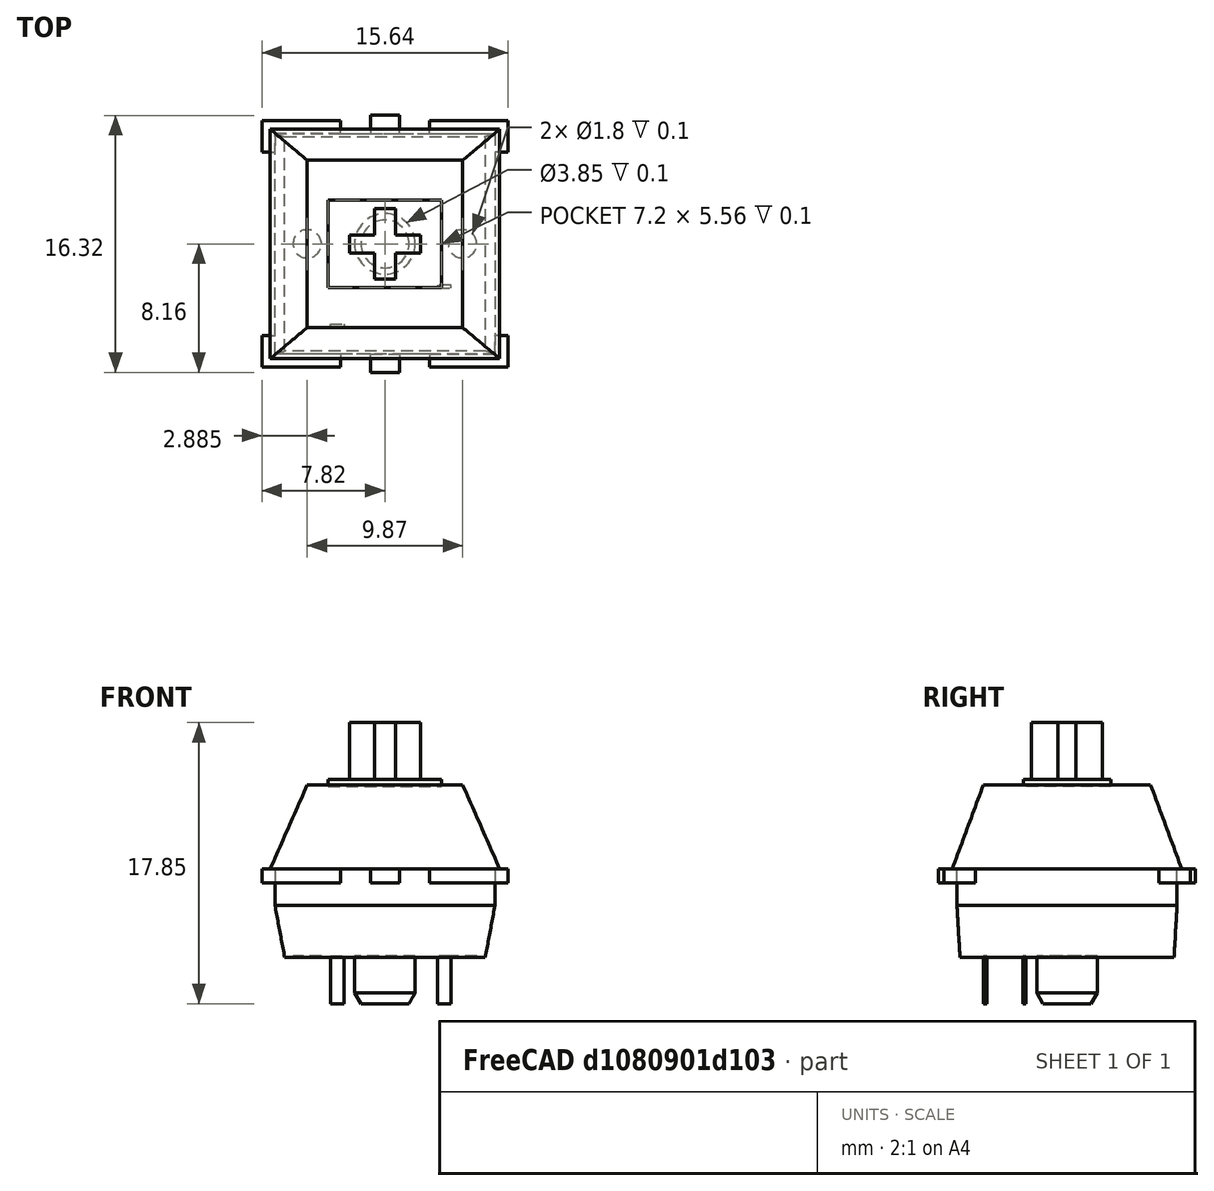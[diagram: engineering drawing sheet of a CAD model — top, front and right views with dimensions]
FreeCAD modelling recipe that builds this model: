
FCSTD DOCUMENT  (FreeCAD 0.19R19285 (Git))
Label: cherry-mx-basic
License: CreativeCommons Attribution-ShareAlike
LicenseURL: http://creativecommons.org/licenses/by-sa/4.0/
objects: Sketcher::SketchObject×20, PartDesign::Pad×7, PartDesign::Pocket×4, PartDesign::Body×4, PartDesign::Plane×3, PartDesign::AdditiveLoft×3, PartDesign::Mirrored×3, PartDesign::MultiTransform×1, Mesh::Feature×1, Part::Feature×1, App::Part×1
note: 60 computed .brp shape members not serialized (recipe doc carries the construction recipe); baked Part::Feature solids carry a one-line shape summary decoded from their .brp

FEATURE [Sketcher::SketchObject] Sketch  label="Master_h"
  MapMode = 5
  Support = -> [XY_Plane]
  sketch-geometry (31):
    g0: LineSegment StartX=7.29 StartY=7.29 StartZ=0 EndX=7.29 EndY=-7.29 EndZ=0
    g1: LineSegment StartX=7.29 StartY=-7.29 StartZ=0 EndX=-7.29 EndY=-7.29 EndZ=0
    g2: LineSegment StartX=-7.29 StartY=-7.29 StartZ=0 EndX=-7.29 EndY=7.29 EndZ=0
    g3: LineSegment StartX=-7.29 StartY=7.29 StartZ=0 EndX=7.29 EndY=7.29 EndZ=0
    g4: LineSegment [constr] StartX=-7.29 StartY=7.29 StartZ=0 EndX=-6.99 EndY=6.99 EndZ=0
    g5: LineSegment StartX=-6.99 StartY=6.99 StartZ=0 EndX=6.99 EndY=6.99 EndZ=0
    g6: LineSegment StartX=6.99 StartY=6.99 StartZ=0 EndX=6.99 EndY=-6.99 EndZ=0
    g7: LineSegment StartX=6.99 StartY=-6.99 StartZ=0 EndX=-6.99 EndY=-6.99 EndZ=0
    g8: LineSegment StartX=-6.99 StartY=-6.99 StartZ=0 EndX=-6.99 EndY=6.99 EndZ=0
    g9: LineSegment StartX=-6.37 StartY=6.8 StartZ=0 EndX=6.37 EndY=6.8 EndZ=0
    g10: LineSegment StartX=6.37 StartY=6.8 StartZ=0 EndX=6.37 EndY=-6.8 EndZ=0
    g11: LineSegment StartX=6.37 StartY=-6.8 StartZ=0 EndX=-6.37 EndY=-6.8 EndZ=0
    g12: LineSegment StartX=-6.37 StartY=-6.8 StartZ=0 EndX=-6.37 EndY=6.8 EndZ=0
    g13: LineSegment StartX=-4.935 StartY=5.31 StartZ=0 EndX=4.935 EndY=5.31 EndZ=0
    g14: LineSegment StartX=4.935 StartY=5.31 StartZ=0 EndX=4.935 EndY=-5.31 EndZ=0
    g15: LineSegment StartX=4.935 StartY=-5.31 StartZ=0 EndX=-4.935 EndY=-5.31 EndZ=0
    g16: LineSegment StartX=-4.935 StartY=-5.31 StartZ=0 EndX=-4.935 EndY=5.31 EndZ=0
    g17: LineSegment StartX=-3.6 StartY=2.78 StartZ=0 EndX=3.6 EndY=2.78 EndZ=0
    g18: LineSegment StartX=3.6 StartY=2.78 StartZ=0 EndX=3.6 EndY=-2.78 EndZ=0
    g19: LineSegment StartX=3.6 StartY=-2.78 StartZ=0 EndX=-3.6 EndY=-2.78 EndZ=0
    g20: LineSegment StartX=-3.6 StartY=-2.78 StartZ=0 EndX=-3.6 EndY=2.78 EndZ=0
    g21: LineSegment StartX=-0.91 StartY=-6.99 StartZ=0 EndX=0.91 EndY=-6.99 EndZ=0
    g22: LineSegment StartX=0.91 StartY=-6.99 StartZ=0 EndX=0.91 EndY=-8.165 EndZ=0
    g23: LineSegment StartX=0.91 StartY=-8.165 StartZ=0 EndX=-0.91 EndY=-8.165 EndZ=0
    g24: LineSegment StartX=-0.91 StartY=-8.165 StartZ=0 EndX=-0.91 EndY=-6.99 EndZ=0
    g25: LineSegment StartX=-7.82 StartY=-5.82 StartZ=0 EndX=-2.82 EndY=-5.82 EndZ=0
    g26: LineSegment StartX=-2.82 StartY=-5.82 StartZ=0 EndX=-2.82 EndY=-7.82 EndZ=0
    g27: LineSegment StartX=-2.82 StartY=-7.82 StartZ=0 EndX=-7.82 EndY=-7.82 EndZ=0
    g28: LineSegment StartX=-7.82 StartY=-7.82 StartZ=0 EndX=-7.82 EndY=-5.82 EndZ=0
    g29: Circle CenterX=0 CenterY=0 CenterZ=0 NormalX=0 NormalY=0 NormalZ=1 AngleXU=0 Radius=1.925
    g30: Circle CenterX=4.935 CenterY=0 CenterZ=0 NormalX=0 NormalY=0 NormalZ=1 AngleXU=0 Radius=0.8
  constraints (85):
    c: Coincident(g0,g1)
    c: Coincident(g1,g2)
    c: Horizontal(g1)
    c: Vertical(g0)
    c: Vertical(g2)
    c: DistanceX(g2,g0) = 14.58
    c: Symmetric(g2,g0,g-1)
    c: Coincident(g3,g2)
    c: Coincident(g3,g0)
    c: Horizontal(g3)
    c: Equal(g3,g0)
    c: Coincident(g4,g2)
    c: Coincident(g5,g6)
    c: Coincident(g6,g7)
    c: Coincident(g7,g8)
    c: Horizontal(g5)
    c: Horizontal(g7)
    c: Vertical(g6)
    c: Vertical(g8)
    c: Symmetric(g5,g6,g-1)
    c: Coincident(g5,g8)
    c: Coincident(g4,g5)
    c: Equal(g5,g8)
    c: DistanceY(g5,g0) = 0.3
    c: Coincident(g9,g10)
    c: Coincident(g10,g11)
    c: Coincident(g11,g12)
    c: Coincident(g12,g9)
    c: Horizontal(g11)
    c: Vertical(g10)
    c: Vertical(g12)
    c: Symmetric(g9,g10,g-1)
    c: Horizontal(g9)
    c: DistanceX(g9,g9) = 12.74
    c: DistanceY(g10,g10) = 13.6
    c: Coincident(g13,g14)
    c: Coincident(g14,g15)
    c: Coincident(g15,g16)
    c: Coincident(g16,g13)
    c: Horizontal(g13)
    c: Horizontal(g15)
    c: Vertical(g14)
    c: Vertical(g16)
    c: Symmetric(g13,g14,g-1)
    c: DistanceX(g13,g13) = 9.87
    c: DistanceY(g16,g16) = 10.62
    c: Coincident(g17,g18)
    c: Coincident(g18,g19)
    c: Coincident(g19,g20)
    c: Coincident(g20,g17)
    c: Horizontal(g17)
    c: Horizontal(g19)
    c: Vertical(g18)
    c: Vertical(g20)
    c: Symmetric(g18,g17,g-1)
    c: DistanceY(g18,g18) = 5.56
    c: DistanceX(g17,g17) = 7.2
    c: Coincident(g21,g22)
    c: Coincident(g22,g23)
    c: Coincident(g23,g24)
    c: Coincident(g24,g21)
    c: Horizontal(g23)
    c: Vertical(g22)
    c: Vertical(g24)
    c: Symmetric(g21,g21,g-2)
    c: PointOnObject(g21,g7)
    c: DistanceX(g23,g23) = 1.82
    c: DistanceY(g22,g22) = 1.175
    c: Coincident(g25,g26)
    c: Coincident(g26,g27)
    c: Coincident(g27,g28)
    c: Coincident(g28,g25)
    c: Horizontal(g25)
    c: Horizontal(g27)
    c: Vertical(g26)
    c: Vertical(g28)
    c: DistanceY(g28,g28) = 2
    c: DistanceX(g25,g25) = 5
    c: DistanceX(g26,g-1) = 2.82
    c: DistanceY(g26,g-1) = 7.82
    c: Coincident(g29,g-1)
    c: Diameter(g29) = 3.85
    c: PointOnObject(g30,g-1)
    c: PointOnObject(g30,g14)
    c: Diameter(g30) = 1.6
FEATURE [Sketcher::SketchObject] Sketch001  label="Master_v"
  MapMode = 5
  Placement = pos=(0,0,0) rot=(1,0,0;1.5708rad)
  Support = -> [XZ_Plane]
  sketch-geometry (4):
    g0: LineSegment StartX=0 StartY=0 StartZ=0 EndX=0 EndY=-2.3 EndZ=0
    g1: LineSegment StartX=0 StartY=-2.3 StartZ=0 EndX=0 EndY=-5.6 EndZ=0
    g2: LineSegment StartX=0 StartY=5.35 StartZ=0 EndX=0 EndY=0 EndZ=0
    g3: LineSegment StartX=8.3181 StartY=0 StartZ=0 EndX=8.3181 EndY=-0.87 EndZ=0
  constraints (12):
    c: Coincident(g0,g-1)
    c: PointOnObject(g0,g-2)
    c: DistanceY(g0,g0) = 2.3  'h1'
    c: Coincident(g1,g0)
    c: Vertical(g1)
    c: DistanceY(g1,g1) = 3.3  'h2'
    c: Coincident(g2,g0)
    c: PointOnObject(g2,g-2)
    c: DistanceY(g2,g2) = 5.35  'h3'
    c: PointOnObject(g3,g-1)
    c: Vertical(g3)
    c: DistanceY(g3,g3) = 0.87  'h4'
FEATURE [PartDesign::Plane] DatumPlane  label="h1_plane"
  AttachmentOffset = pos=(0,0,-2.3) rot=(0,0,1;0rad)
  Length = 60
  MapMode = 5
  Placement = pos=(0,0,-2.3) rot=(0,0,1;0rad)
  ResizeMode = 0
  Support = -> [XY_Plane]
  Width = 60
  expr: .AttachmentOffset.Base.z = -<<Master_v>>.Constraints.h1
FEATURE [Sketcher::SketchObject] Sketch002  label="bottom_p1_sketch"
  ExternalGeometry = -> [Sketch]
  MapMode = 5
  Support = -> [XY_Plane]
  sketch-geometry (4):
    g0: LineSegment StartX=-6.99 StartY=6.99 StartZ=0 EndX=6.99 EndY=6.99 EndZ=0
    g1: LineSegment StartX=6.99 StartY=6.99 StartZ=0 EndX=6.99 EndY=-6.99 EndZ=0
    g2: LineSegment StartX=6.99 StartY=-6.99 StartZ=0 EndX=-6.99 EndY=-6.99 EndZ=0
    g3: LineSegment StartX=-6.99 StartY=-6.99 StartZ=0 EndX=-6.99 EndY=6.99 EndZ=0
  constraints (10):
    c: Coincident(g0,g1)
    c: Coincident(g1,g2)
    c: Coincident(g2,g3)
    c: Coincident(g3,g0)
    c: Horizontal(g0)
    c: Horizontal(g2)
    c: Vertical(g1)
    c: Vertical(g3)
    c: Coincident(g0,g-3)
    c: Coincident(g1,g-4)
FEATURE [PartDesign::Pad] Pad  label="bottom_p1"
  Length = 2.3
  Length2 = 100
  Profile = -> Sketch002
  Refine = true
  Reversed = true
  Type = 0
  expr: Length = <<Master_v>>.Constraints.h1
FEATURE [PartDesign::Plane] DatumPlane001  label="Bottom_plane"
  AttachmentOffset = pos=(0,0,-5.6) rot=(0,0,1;0rad)
  Length = 60
  MapMode = 5
  Placement = pos=(0,0,-5.6) rot=(0,0,1;0rad)
  ResizeMode = 0
  Support = -> [XY_Plane]
  Width = 60
  expr: .AttachmentOffset.Base.z = -<<Master_v>>.Constraints.h2 - <<Master_v>>.Constraints.h1
FEATURE [Sketcher::SketchObject] Sketch003  label="bottom_p2_bott_sketch"
  ExternalGeometry = -> [Sketch]
  MapMode = 5
  Placement = pos=(0,0,-5.6) rot=(0,0,1;0rad)
  Support = -> [DatumPlane001]
  sketch-geometry (4):
    g0: LineSegment StartX=-6.37 StartY=6.8 StartZ=0 EndX=6.37 EndY=6.8 EndZ=0
    g1: LineSegment StartX=6.37 StartY=6.8 StartZ=0 EndX=6.37 EndY=-6.8 EndZ=0
    g2: LineSegment StartX=6.37 StartY=-6.8 StartZ=0 EndX=-6.37 EndY=-6.8 EndZ=0
    g3: LineSegment StartX=-6.37 StartY=-6.8 StartZ=0 EndX=-6.37 EndY=6.8 EndZ=0
  constraints (10):
    c: Coincident(g0,g1)
    c: Coincident(g1,g2)
    c: Coincident(g2,g3)
    c: Coincident(g3,g0)
    c: Horizontal(g0)
    c: Horizontal(g2)
    c: Vertical(g1)
    c: Vertical(g3)
    c: Symmetric(g0,g1,g-1)
    c: Coincident(g0,g-3)
FEATURE [Sketcher::SketchObject] Sketch004  label="bottom_p2_top_sketch"
  ExternalGeometry = -> [Sketch]
  MapMode = 5
  Placement = pos=(0,0,-2.3) rot=(0,0,1;0rad)
  Support = -> [DatumPlane]
  sketch-geometry (4):
    g0: LineSegment StartX=-6.99 StartY=6.99 StartZ=0 EndX=6.99 EndY=6.99 EndZ=0
    g1: LineSegment StartX=6.99 StartY=6.99 StartZ=0 EndX=6.99 EndY=-6.99 EndZ=0
    g2: LineSegment StartX=6.99 StartY=-6.99 StartZ=0 EndX=-6.99 EndY=-6.99 EndZ=0
    g3: LineSegment StartX=-6.99 StartY=-6.99 StartZ=0 EndX=-6.99 EndY=6.99 EndZ=0
  constraints (10):
    c: Coincident(g0,g1)
    c: Coincident(g1,g2)
    c: Coincident(g2,g3)
    c: Coincident(g3,g0)
    c: Horizontal(g0)
    c: Horizontal(g2)
    c: Vertical(g1)
    c: Vertical(g3)
    c: Symmetric(g0,g1,g-1)
    c: Coincident(g0,g-3)
FEATURE [PartDesign::AdditiveLoft] AdditiveLoft  label="bottom_p2"
  BaseFeature = -> Pad
  Closed = false
  Profile = -> Sketch004
  Refine = true
  Ruled = false
  Sections = -> [Sketch003]
FEATURE [Sketcher::SketchObject] Sketch005  label="top_p1_sketch"
  ExternalGeometry = -> [Sketch]
  MapMode = 5
  Support = -> [XY_Plane]
  sketch-geometry (4):
    g0: LineSegment StartX=-7.29 StartY=7.29 StartZ=0 EndX=7.29 EndY=7.29 EndZ=0
    g1: LineSegment StartX=7.29 StartY=7.29 StartZ=0 EndX=7.29 EndY=-7.29 EndZ=0
    g2: LineSegment StartX=7.29 StartY=-7.29 StartZ=0 EndX=-7.29 EndY=-7.29 EndZ=0
    g3: LineSegment StartX=-7.29 StartY=-7.29 StartZ=0 EndX=-7.29 EndY=7.29 EndZ=0
  constraints (10):
    c: Coincident(g0,g1)
    c: Coincident(g1,g2)
    c: Coincident(g2,g3)
    c: Coincident(g3,g0)
    c: Horizontal(g0)
    c: Horizontal(g2)
    c: Vertical(g1)
    c: Vertical(g3)
    c: Symmetric(g0,g1,g-1)
    c: Coincident(g0,g-3)
FEATURE [PartDesign::Plane] DatumPlane002  label="h3_plane"
  AttachmentOffset = pos=(0,0,5.35) rot=(0,0,1;0rad)
  Length = 60
  MapMode = 5
  Placement = pos=(0,0,5.35) rot=(0,0,1;0rad)
  ResizeMode = 0
  Support = -> [XY_Plane]
  Width = 60
  expr: .AttachmentOffset.Base.z = <<Master_v>>.Constraints.h3
FEATURE [Sketcher::SketchObject] Sketch006  label="top_p1_sketch2"
  ExternalGeometry = -> [Sketch]
  MapMode = 5
  Placement = pos=(0,0,5.35) rot=(0,0,1;0rad)
  Support = -> [DatumPlane002]
  sketch-geometry (4):
    g0: LineSegment StartX=-4.935 StartY=5.31 StartZ=0 EndX=4.935 EndY=5.31 EndZ=0
    g1: LineSegment StartX=4.935 StartY=5.31 StartZ=0 EndX=4.935 EndY=-5.31 EndZ=0
    g2: LineSegment StartX=4.935 StartY=-5.31 StartZ=0 EndX=-4.935 EndY=-5.31 EndZ=0
    g3: LineSegment StartX=-4.935 StartY=-5.31 StartZ=0 EndX=-4.935 EndY=5.31 EndZ=0
  constraints (10):
    c: Coincident(g0,g1)
    c: Coincident(g1,g2)
    c: Coincident(g2,g3)
    c: Coincident(g3,g0)
    c: Horizontal(g0)
    c: Horizontal(g2)
    c: Vertical(g1)
    c: Vertical(g3)
    c: Symmetric(g0,g1,g-1)
    c: Coincident(g0,g-3)
FEATURE [PartDesign::AdditiveLoft] AdditiveLoft001  label="top"
  BaseFeature = -> AdditiveLoft
  Closed = false
  Profile = -> Sketch005
  Refine = true
  Ruled = false
  Sections = -> [Sketch006]
FEATURE [Sketcher::SketchObject] Sketch007  label="axis_cutout_sketch"
  ExternalGeometry = -> [Sketch]
  MapMode = 5
  Placement = pos=(0,0,5.35) rot=(0,0,1;0rad)
  Support = -> [DatumPlane002]
  sketch-geometry (4):
    g0: LineSegment StartX=-3.6 StartY=2.78 StartZ=0 EndX=3.6 EndY=2.78 EndZ=0
    g1: LineSegment StartX=3.6 StartY=2.78 StartZ=0 EndX=3.6 EndY=-2.78 EndZ=0
    g2: LineSegment StartX=3.6 StartY=-2.78 StartZ=0 EndX=-3.6 EndY=-2.78 EndZ=0
    g3: LineSegment StartX=-3.6 StartY=-2.78 StartZ=0 EndX=-3.6 EndY=2.78 EndZ=0
  constraints (10):
    c: Coincident(g0,g1)
    c: Coincident(g1,g2)
    c: Coincident(g2,g3)
    c: Coincident(g3,g0)
    c: Horizontal(g0)
    c: Horizontal(g2)
    c: Vertical(g1)
    c: Vertical(g3)
    c: Coincident(g0,g-3)
    c: Symmetric(g0,g1,g-1)
FEATURE [PartDesign::Pocket] Pocket  label="top_axis_cutout"
  BaseFeature = -> AdditiveLoft001
  Length = 0.1
  Length2 = 100
  Profile = -> Sketch007
  Refine = true
  Type = 0
FEATURE [Sketcher::SketchObject] Sketch008  label="middle-ear-sketch"
  ExternalGeometry = -> [Sketch]
  MapMode = 5
  Support = -> [XY_Plane]
  sketch-geometry (4):
    g0: LineSegment StartX=-0.91 StartY=-6.99 StartZ=0 EndX=0.91 EndY=-6.99 EndZ=0
    g1: LineSegment StartX=0.91 StartY=-6.99 StartZ=0 EndX=0.91 EndY=-8.165 EndZ=0
    g2: LineSegment StartX=0.91 StartY=-8.165 StartZ=0 EndX=-0.91 EndY=-8.165 EndZ=0
    g3: LineSegment StartX=-0.91 StartY=-8.165 StartZ=0 EndX=-0.91 EndY=-6.99 EndZ=0
  constraints (10):
    c: Coincident(g0,g1)
    c: Coincident(g1,g2)
    c: Coincident(g2,g3)
    c: Coincident(g3,g0)
    c: Horizontal(g0)
    c: Horizontal(g2)
    c: Vertical(g1)
    c: Vertical(g3)
    c: Coincident(g0,g-3)
    c: Coincident(g1,g-4)
FEATURE [PartDesign::Pad] Pad001  label="middle-ear"
  BaseFeature = -> Pocket
  Length = 0.87
  Length2 = 100
  Profile = -> Sketch008
  Refine = true
  Reversed = true
  Type = 0
  expr: Length = <<Master_v>>.Constraints.h4
FEATURE [Sketcher::SketchObject] Sketch009  label="corner-ear-sketch"
  ExternalGeometry = -> [Sketch]
  MapMode = 5
  Support = -> [XY_Plane]
  sketch-geometry (4):
    g0: LineSegment StartX=-7.82 StartY=-5.82 StartZ=0 EndX=-2.82 EndY=-5.82 EndZ=0
    g1: LineSegment StartX=-2.82 StartY=-5.82 StartZ=0 EndX=-2.82 EndY=-7.82 EndZ=0
    g2: LineSegment StartX=-2.82 StartY=-7.82 StartZ=0 EndX=-7.82 EndY=-7.82 EndZ=0
    g3: LineSegment StartX=-7.82 StartY=-7.82 StartZ=0 EndX=-7.82 EndY=-5.82 EndZ=0
  constraints (10):
    c: Coincident(g0,g1)
    c: Coincident(g1,g2)
    c: Coincident(g2,g3)
    c: Coincident(g3,g0)
    c: Horizontal(g0)
    c: Horizontal(g2)
    c: Vertical(g1)
    c: Vertical(g3)
    c: Coincident(g0,g-4)
    c: Coincident(g1,g-5)
FEATURE [PartDesign::Pad] Pad002  label="corner-ear"
  BaseFeature = -> Pad001
  Length = 0.87
  Length2 = 100
  Profile = -> Sketch009
  Refine = true
  Reversed = true
  Type = 0
  expr: Length = <<Master_v>>.Constraints.h4
FEATURE [PartDesign::Mirrored] Mirrored
  MirrorPlane = -> YZ_Plane
  Refine = true
FEATURE [PartDesign::Mirrored] Mirrored001
  MirrorPlane = -> XZ_Plane
  Refine = true
FEATURE [PartDesign::MultiTransform] MultiTransform  label="corner-ears"
  BaseFeature = -> Pad002
  Originals = -> [Pad002]
  Refine = true
  Transformations = -> [Mirrored,Mirrored001]
FEATURE [PartDesign::Mirrored] Mirrored002  label="middle-ears"
  BaseFeature = -> MultiTransform
  MirrorPlane = -> XZ_Plane
  Originals = -> [Pad001]
  Refine = true
FEATURE [Sketcher::SketchObject] Sketch010  label="central-peg-sketch"
  ExternalGeometry = -> [Sketch]
  MapMode = 5
  Placement = pos=(0,0,-5.6) rot=(0,0,1;0rad)
  Support = -> [DatumPlane001]
  sketch-geometry (1):
    g0: Circle CenterX=0 CenterY=0 CenterZ=0 NormalX=0 NormalY=0 NormalZ=1 AngleXU=0 Radius=1.925
  constraints (1):
    c: Coincident(g0,g-1)
FEATURE [PartDesign::Pocket] Pocket001  label="central-peg"
  BaseFeature = -> Mirrored002
  Length = 0.1
  Length2 = 100
  Profile = -> Sketch010
  Refine = true
  Reversed = true
  Type = 0
FEATURE [Sketcher::SketchObject] Sketch011  label="pegs-sketch"
  ExternalGeometry = -> [Sketch]
  MapMode = 5
  Placement = pos=(0,0,-5.6) rot=(0,0,1;0rad)
  Support = -> [DatumPlane001]
  sketch-geometry (2):
    g0: Circle CenterX=4.935 CenterY=0 CenterZ=0 NormalX=0 NormalY=0 NormalZ=1 AngleXU=0 Radius=0.9
    g1: Circle CenterX=-4.935 CenterY=0 CenterZ=0 NormalX=0 NormalY=0 NormalZ=1 AngleXU=0 Radius=0.9
  constraints (2):
    c: Symmetric(g1,g0,g-2)
    c: Equal(g1,g0)
FEATURE [PartDesign::Pocket] Pocket002  label="pegs"
  BaseFeature = -> Pocket001
  Length = 0.1
  Length2 = 100
  Profile = -> Sketch011
  Refine = true
  Reversed = true
  Type = 0
FEATURE [Sketcher::SketchObject] Sketch012  label="pins_sketch"
  MapMode = 5
  Placement = pos=(0,0,-5.6) rot=(0,0,1;0rad)
  Support = -> [DatumPlane001]
  sketch-geometry (8):
    g0: LineSegment StartX=-3.46 StartY=-5.1 StartZ=0 EndX=-2.6 EndY=-5.1 EndZ=0
    g1: LineSegment StartX=-2.6 StartY=-5.1 StartZ=0 EndX=-2.6 EndY=-5.3 EndZ=0
    g2: LineSegment StartX=-2.6 StartY=-5.3 StartZ=0 EndX=-3.46 EndY=-5.3 EndZ=0
    g3: LineSegment StartX=-3.46 StartY=-5.3 StartZ=0 EndX=-3.46 EndY=-5.1 EndZ=0
    g4: LineSegment StartX=3.34 StartY=-2.8 StartZ=0 EndX=4.2 EndY=-2.8 EndZ=0
    g5: LineSegment StartX=4.2 StartY=-2.8 StartZ=0 EndX=4.2 EndY=-2.6 EndZ=0
    g6: LineSegment StartX=4.2 StartY=-2.6 StartZ=0 EndX=3.34 EndY=-2.6 EndZ=0
    g7: LineSegment StartX=3.34 StartY=-2.6 StartZ=0 EndX=3.34 EndY=-2.8 EndZ=0
  constraints (24):
    c: Coincident(g0,g1)
    c: Coincident(g1,g2)
    c: Coincident(g2,g3)
    c: Coincident(g3,g0)
    c: Horizontal(g0)
    c: Horizontal(g2)
    c: Vertical(g1)
    c: Vertical(g3)
    c: DistanceX(g0,g0) = 0.86
    c: DistanceY(g1,g1) = 0.2
    c: DistanceX(g0,g-1) = 2.6
    c: DistanceY(g0,g-1) = 5.1
    c: Coincident(g4,g5)
    c: Coincident(g5,g6)
    c: Coincident(g6,g7)
    c: Coincident(g7,g4)
    c: Horizontal(g4)
    c: Horizontal(g6)
    c: Vertical(g5)
    c: Vertical(g7)
    c: Equal(g1,g7)
    c: Equal(g0,g4)
    c: DistanceX(g-1,g4) = 3.34
    c: DistanceY(g6,g-1) = 2.6
FEATURE [PartDesign::Pocket] Pocket003  label="pins"
  BaseFeature = -> Pocket002
  Length = 0.1
  Length2 = 100
  Profile = -> Sketch012
  Refine = true
  Reversed = true
  Type = 0
FEATURE [PartDesign::Body] Body  label="cherry-body"
  Group = -> [Sketch,Sketch001,DatumPlane,Sketch002,Pad,Sketch003,DatumPlane001,Sketch004,AdditiveLoft,Sketch005,DatumPlane002,Sketch006,AdditiveLoft001,Sketch007,Pocket,Sketch008,Pad001,Sketch009,Pad002,MultiTransform,Mirrored,Mirrored001,Mirrored002,Sketch010,Pocket001,Sketch011,Pocket002,Sketch012,Pocket003]
  Origin = -> Origin
  Tip = -> Pocket003
FEATURE [Sketcher::SketchObject] Sketch013  label="master_h"
  MapMode = 5
  Support = -> [XY_Plane001]
  sketch-geometry (16):
    g0: LineSegment StartX=-3.6 StartY=2.78 StartZ=0 EndX=3.6 EndY=2.78 EndZ=0
    g1: LineSegment StartX=3.6 StartY=2.78 StartZ=0 EndX=3.6 EndY=-2.78 EndZ=0
    g2: LineSegment StartX=3.6 StartY=-2.78 StartZ=0 EndX=-3.6 EndY=-2.78 EndZ=0
    g3: LineSegment StartX=-3.6 StartY=-2.78 StartZ=0 EndX=-3.6 EndY=2.78 EndZ=0
    g4: LineSegment StartX=-2.25 StartY=-0.575 StartZ=0 EndX=-2.25 EndY=0.575 EndZ=0
    g5: LineSegment StartX=-2.25 StartY=0.575 StartZ=0 EndX=-0.675 EndY=0.575 EndZ=0
    g6: LineSegment StartX=-0.675 StartY=0.575 StartZ=0 EndX=-0.675 EndY=2.25 EndZ=0
    g7: LineSegment StartX=-0.675 StartY=2.25 StartZ=0 EndX=0.675 EndY=2.25 EndZ=0
    g8: LineSegment StartX=-2.25 StartY=-0.575 StartZ=0 EndX=-0.675 EndY=-0.575 EndZ=0
    g9: LineSegment StartX=-0.675 StartY=-0.575 StartZ=0 EndX=-0.675 EndY=-2.25 EndZ=0
    g10: LineSegment StartX=-0.675 StartY=-2.25 StartZ=0 EndX=0.675 EndY=-2.25 EndZ=0
    g11: LineSegment StartX=0.675 StartY=-2.25 StartZ=0 EndX=0.675 EndY=-0.575 EndZ=0
    g12: LineSegment StartX=0.675 StartY=-0.575 StartZ=0 EndX=2.25 EndY=-0.575 EndZ=0
    g13: LineSegment StartX=2.25 StartY=-0.575 StartZ=0 EndX=2.25 EndY=0.575 EndZ=0
    g14: LineSegment StartX=2.25 StartY=0.575 StartZ=0 EndX=0.675 EndY=0.575 EndZ=0
    g15: LineSegment StartX=0.675 StartY=0.575 StartZ=0 EndX=0.675 EndY=2.25 EndZ=0
  constraints (38):
    c: Coincident(g0,g1)
    c: Coincident(g1,g2)
    c: Coincident(g2,g3)
    c: Horizontal(g0)
    c: Horizontal(g2)
    c: Vertical(g1)
    c: Vertical(g3)
    c: DistanceX(g0,g0) = 7.2
    c: DistanceY(g1,g1) = 5.56
    c: Symmetric(g0,g1,g-1)
    c: Coincident(g4,g5)
    c: Horizontal(g5)
    c: Coincident(g5,g6)
    c: Vertical(g6)
    c: Coincident(g6,g7)
    c: DistanceX(g7,g7) = 1.35
    c: DistanceX(g5,g5) = 1.575
    c: DistanceY(g6,g6) = 1.675
    c: DistanceY(g4,g4) = 1.15
    c: Coincident(g4,g8)
    c: Coincident(g8,g9)
    c: Coincident(g9,g10)
    c: Coincident(g10,g11)
    c: Coincident(g11,g12)
    c: Coincident(g12,g13)
    c: Coincident(g13,g14)
    c: Coincident(g14,g15)
    c: Coincident(g15,g7)
    c: Symmetric(g7,g6,g-2)
    c: Symmetric(g14,g5,g-2)
    c: Symmetric(g13,g4,g-2)
    c: Symmetric(g12,g4,g-2)
    c: Symmetric(g8,g11,g-2)
    c: Symmetric(g10,g9,g-2)
    c: Symmetric(g4,g4,g-1)
    c: Symmetric(g8,g5,g-1)
    c: Symmetric(g9,g6,g-1)
    c: Coincident(g3,g0)
FEATURE [Sketcher::SketchObject] Sketch014  label="master_v"
  MapMode = 5
  Placement = pos=(0,0,0) rot=(1,0,0;1.5708rad)
  Support = -> [XZ_Plane001]
  sketch-geometry (2):
    g0: LineSegment StartX=0 StartY=0 StartZ=0 EndX=0 EndY=0.43 EndZ=0
    g1: LineSegment StartX=0 StartY=0.43 StartZ=0 EndX=0 EndY=4.05 EndZ=0
  constraints (6):
    c: Coincident(g0,g-1)
    c: Vertical(g0)
    c: DistanceY(g0,g0) = 0.43  'h1'
    c: Coincident(g1,g0)
    c: PointOnObject(g1,g-2)
    c: DistanceY(g1,g1) = 3.62  'h2'
FEATURE [Sketcher::SketchObject] Sketch015
  MapMode = 5
  Support = -> [XY_Plane001]
  expr: Constraints[7] = Sketch013.Constraints[7]
  expr: Constraints[8] = Sketch013.Constraints[8]
  sketch-geometry (4):
    g0: LineSegment StartX=-3.6 StartY=2.78 StartZ=0 EndX=3.6 EndY=2.78 EndZ=0
    g1: LineSegment StartX=3.6 StartY=2.78 StartZ=0 EndX=3.6 EndY=-2.78 EndZ=0
    g2: LineSegment StartX=3.6 StartY=-2.78 StartZ=0 EndX=-3.6 EndY=-2.78 EndZ=0
    g3: LineSegment StartX=-3.6 StartY=-2.78 StartZ=0 EndX=-3.6 EndY=2.78 EndZ=0
  constraints (11):
    c: Coincident(g0,g1)
    c: Coincident(g1,g2)
    c: Coincident(g2,g3)
    c: Horizontal(g0)
    c: Horizontal(g2)
    c: Vertical(g1)
    c: Vertical(g3)
    c: DistanceX(g0,g0) = 7.2
    c: DistanceY(g1,g1) = 5.56
    c: Symmetric(g0,g1,g-1)
    c: Coincident(g3,g0)
FEATURE [PartDesign::Pad] Pad003  label="Base"
  Length = 0.43
  Length2 = 100
  Profile = -> Sketch015
  Refine = true
  Type = 0
  expr: Length = <<master_v>>.Constraints.h1
FEATURE [Sketcher::SketchObject] Sketch016
  AttachmentOffset = pos=(0,0,0.43) rot=(0,0,1;0rad)
  MapMode = 5
  Placement = pos=(0,0,0.43) rot=(0,0,1;0rad)
  Support = -> [XY_Plane001]
  expr: Constraints[8] = Sketch013.Constraints[18]
  expr: Constraints[5] = Sketch013.Constraints[15]
  expr: .AttachmentOffset.Base.z = <<master_v>>.Constraints.h1
  expr: Constraints[7] = Sketch013.Constraints[17]
  expr: Constraints[6] = Sketch013.Constraints[16]
  sketch-geometry (12):
    g0: LineSegment StartX=-2.25 StartY=-0.575 StartZ=0 EndX=-2.25 EndY=0.575 EndZ=0
    g1: LineSegment StartX=-2.25 StartY=0.575 StartZ=0 EndX=-0.675 EndY=0.575 EndZ=0
    g2: LineSegment StartX=-0.675 StartY=0.575 StartZ=0 EndX=-0.675 EndY=2.25 EndZ=0
    g3: LineSegment StartX=-0.675 StartY=2.25 StartZ=0 EndX=0.675 EndY=2.25 EndZ=0
    g4: LineSegment StartX=-2.25 StartY=-0.575 StartZ=0 EndX=-0.675 EndY=-0.575 EndZ=0
    g5: LineSegment StartX=-0.675 StartY=-0.575 StartZ=0 EndX=-0.675 EndY=-2.25 EndZ=0
    g6: LineSegment StartX=-0.675 StartY=-2.25 StartZ=0 EndX=0.675 EndY=-2.25 EndZ=0
    g7: LineSegment StartX=0.675 StartY=-2.25 StartZ=0 EndX=0.675 EndY=-0.575 EndZ=0
    g8: LineSegment StartX=0.675 StartY=-0.575 StartZ=0 EndX=2.25 EndY=-0.575 EndZ=0
    g9: LineSegment StartX=2.25 StartY=-0.575 StartZ=0 EndX=2.25 EndY=0.575 EndZ=0
    g10: LineSegment StartX=2.25 StartY=0.575 StartZ=0 EndX=0.675 EndY=0.575 EndZ=0
    g11: LineSegment StartX=0.675 StartY=0.575 StartZ=0 EndX=0.675 EndY=2.25 EndZ=0
  constraints (27):
    c: Coincident(g0,g1)
    c: Horizontal(g1)
    c: Coincident(g1,g2)
    c: Vertical(g2)
    c: Coincident(g2,g3)
    c: DistanceX(g3,g3) = 1.35
    c: DistanceX(g1,g1) = 1.575
    c: DistanceY(g2,g2) = 1.675
    c: DistanceY(g0,g0) = 1.15
    c: Coincident(g0,g4)
    c: Coincident(g4,g5)
    c: Coincident(g5,g6)
    c: Coincident(g6,g7)
    c: Coincident(g7,g8)
    c: Coincident(g8,g9)
    c: Coincident(g9,g10)
    c: Coincident(g10,g11)
    c: Coincident(g11,g3)
    c: Symmetric(g3,g2,g-2)
    c: Symmetric(g10,g1,g-2)
    c: Symmetric(g9,g0,g-2)
    c: Symmetric(g8,g0,g-2)
    c: Symmetric(g4,g7,g-2)
    c: Symmetric(g6,g5,g-2)
    c: Symmetric(g0,g0,g-1)
    c: Symmetric(g4,g1,g-1)
    c: Symmetric(g5,g2,g-1)
FEATURE [PartDesign::Pad] Pad004  label="Cross"
  BaseFeature = -> Pad003
  Length = 3.62
  Length2 = 100
  Profile = -> Sketch016
  Refine = true
  Type = 0
  expr: Length = <<master_v>>.Constraints.h2
FEATURE [PartDesign::Body] Body001  label="cherry-axis"
  Group = -> [Sketch013,Sketch014,Sketch015,Pad003,Sketch016,Pad004]
  Origin = -> Origin001
  Placement = pos=(0,0,5.25) rot=(0,0,1;0rad)
  Tip = -> Pad004
FEATURE [Sketcher::SketchObject] Sketch017  label="base_small"
  MapMode = 5
  Support = -> [XY_Plane002]
  sketch-geometry (1):
    g0: Circle CenterX=0 CenterY=0 CenterZ=0 NormalX=0 NormalY=0 NormalZ=1 AngleXU=0 Radius=1.525
  constraints (2):
    c: Radius(g0) = 1.525
    c: Coincident(g0,g-1)
FEATURE [Sketcher::SketchObject] Sketch018  label="base"
  AttachmentOffset = pos=(0,0,0.69) rot=(0,0,1;0rad)
  MapMode = 5
  Placement = pos=(0,0,0.69) rot=(0,0,1;0rad)
  Support = -> [XY_Plane002]
  sketch-geometry (1):
    g0: Circle CenterX=0 CenterY=0 CenterZ=0 NormalX=0 NormalY=0 NormalZ=1 AngleXU=0 Radius=1.925
  constraints (2):
    c: Radius(g0) = 1.925
    c: Coincident(g0,g-1)
FEATURE [PartDesign::AdditiveLoft] AdditiveLoft002
  Closed = false
  Profile = -> Sketch017
  Refine = true
  Ruled = false
  Sections = -> [Sketch018]
FEATURE [PartDesign::Pad] Pad005  label="peg"
  BaseFeature = -> AdditiveLoft002
  Length = 2.36
  Length2 = 100
  Profile = -> Sketch018
  Refine = true
  Type = 0
FEATURE [PartDesign::Body] Body002  label="cherry-peg"
  Group = -> [Sketch017,Sketch018,AdditiveLoft002,Pad005]
  Origin = -> Origin002
  Placement = pos=(0,0,-8.55) rot=(0,0,1;0rad)
  Tip = -> Pad005
FEATURE [Sketcher::SketchObject] Sketch019
  MapMode = 5
  Support = -> [XY_Plane003]
  sketch-geometry (4):
    g0: LineSegment StartX=-0.43 StartY=0.1 StartZ=0 EndX=0.43 EndY=0.1 EndZ=0
    g1: LineSegment StartX=0.43 StartY=0.1 StartZ=0 EndX=0.43 EndY=-0.1 EndZ=0
    g2: LineSegment StartX=0.43 StartY=-0.1 StartZ=0 EndX=-0.43 EndY=-0.1 EndZ=0
    g3: LineSegment StartX=-0.43 StartY=-0.1 StartZ=0 EndX=-0.43 EndY=0.1 EndZ=0
  constraints (11):
    c: Coincident(g0,g1)
    c: Coincident(g1,g2)
    c: Coincident(g2,g3)
    c: Coincident(g3,g0)
    c: Horizontal(g0)
    c: Horizontal(g2)
    c: Vertical(g1)
    c: Vertical(g3)
    c: DistanceX(g0,g0) = 0.86
    c: DistanceY(g1,g1) = 0.2
    c: Symmetric(g0,g1,g-1)
FEATURE [PartDesign::Pad] Pad006
  Length = 3.05
  Length2 = 100
  Profile = -> Sketch019
  Refine = true
  Type = 0
FEATURE [PartDesign::Body] Body003  label="pin1"
  Group = -> [Sketch019,Pad006]
  Origin = -> Origin003
  Placement = pos=(-3.03,-5.2,-8.55) rot=(0,0,1;0rad)
  Tip = -> Pad006
FEATURE [Mesh::Feature] Mesh  label="cherry-mx-basic (Meshed)"
FEATURE [Part::Feature] Body003001  label="pin002"
  Placement = pos=(3.77,-2.7,-8.55) rot=(0,0,1;0rad)
  shape: bbox 0.86 x 0.2 x 3.05 mm, 6 faces (baked)
FEATURE [App::Part] Part  label="cherry-mx-basic"
  Group = -> [Body,Body001,Body002,Body003,Body003001]
  Origin = -> Origin005
